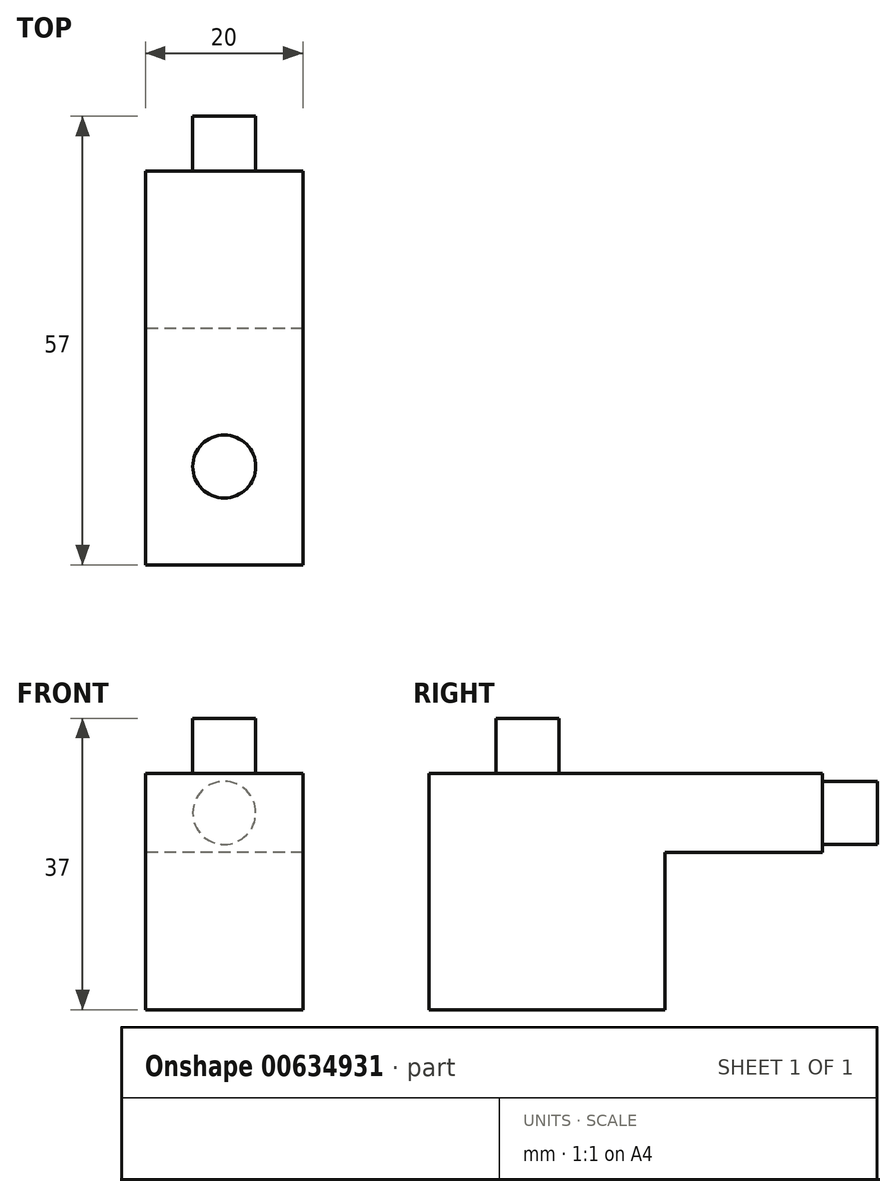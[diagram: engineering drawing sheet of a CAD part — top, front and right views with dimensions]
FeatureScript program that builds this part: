
annotation { "Feature Type Name" : "Feature", "Feature Type Description" : "" }
export const myFeature = defineFeature(function(context is Context, id is Id, definition is map)
    precondition{}
    {
        {
            var Q0;
            Q0=qCreatedBy(makeId("Right.planeOp"),FACE);
            var sketch = newSketch(context, id + "F0", { "sketchPlane" : qUnion([Q0])});
            skLineSegment(sketch, "E0", {"start": v(0, 0) * mm, "end": v(0, 30) * mm});
            skLineSegment(sketch, "E1", {"start": v(0, 30) * mm, "end": v(50, 30) * mm});
            skLineSegment(sketch, "E2", {"start": v(50, 30) * mm, "end": v(50, 20) * mm});
            skLineSegment(sketch, "E3", {"start": v(50, 20) * mm, "end": v(30, 20) * mm});
            skLineSegment(sketch, "E4", {"start": v(30, 20) * mm, "end": v(30, 0) * mm});
            skLineSegment(sketch, "E5", {"start": v(30, 0) * mm, "end": v(0, 0) * mm});
            skSolve(sketch);
        }
        {
            var Q0;
            Q0 = qSketchRegion(id + "F0", true);
            extrude(context, id + "F1", {"entities" : qUnion([Q0]), "depth" : 20 * mm, "offsetDistance" : 25 * mm});
        }
        {
            var Q0;
            Q0=makeQuery(id+"F1.opExtrude","SWEPT_FACE",FACE,{"disambiguationData":[OSD([sQuery(id+"F0.wireOp",EDGE,"E2")])]});
            var sketch = newSketch(context, id + "F2", { "sketchPlane" : qUnion([Q0])});
            skLineSegment(sketch, "E6", {"start": v(-20, 20) * mm, "end": v(0, 30) * mm, "construction": true});
            skCircle(sketch, "E7", {"center": v(-10, 25) * mm, "radius": 4 * mm});
            skSolve(sketch);
        }
        {
            var Q0;
            Q0=makeQuery(id+"F2.imprint","IMPRINT",FACE,{"disambiguationData":[TD([[makeQuery(id+"F2.imprint","IMPRINT",EDGE,{"derivedFrom":sQuery(id+"F2.wireOp",EDGE,"E7")}),1.0]])]});
            extrude(context, id + "F3", {"entities" : qUnion([Q0]), "operationType" : NewBodyOperationType.ADD, "depth" : 7 * mm, "offsetDistance" : 25 * mm});
        }
        {
            var Q0;
            Q0=makeQuery(id+"F1.opExtrude","SWEPT_FACE",FACE,{"disambiguationData":[OSD([sQuery(id+"F0.wireOp",EDGE,"E1")])]});
            var sketch = newSketch(context, id + "F4", { "sketchPlane" : qUnion([Q0])});
            skLineSegment(sketch, "E8", {"start": v(0, 0) * mm, "end": v(20, 25) * mm, "construction": true});
            skCircle(sketch, "E9", {"center": v(10, 12.5) * mm, "radius": 4 * mm});
            skSolve(sketch);
        }
        {
            var Q0;
            Q0=makeQuery(id+"F4.imprint","IMPRINT",FACE,{"disambiguationData":[TD([[makeQuery(id+"F4.imprint","IMPRINT",EDGE,{"derivedFrom":sQuery(id+"F4.wireOp",EDGE,"E9")}),1.0]])]});
            extrude(context, id + "F5", {"entities" : qUnion([Q0]), "operationType" : NewBodyOperationType.ADD, "depth" : 7 * mm, "offsetDistance" : 25 * mm});
        }
    });
